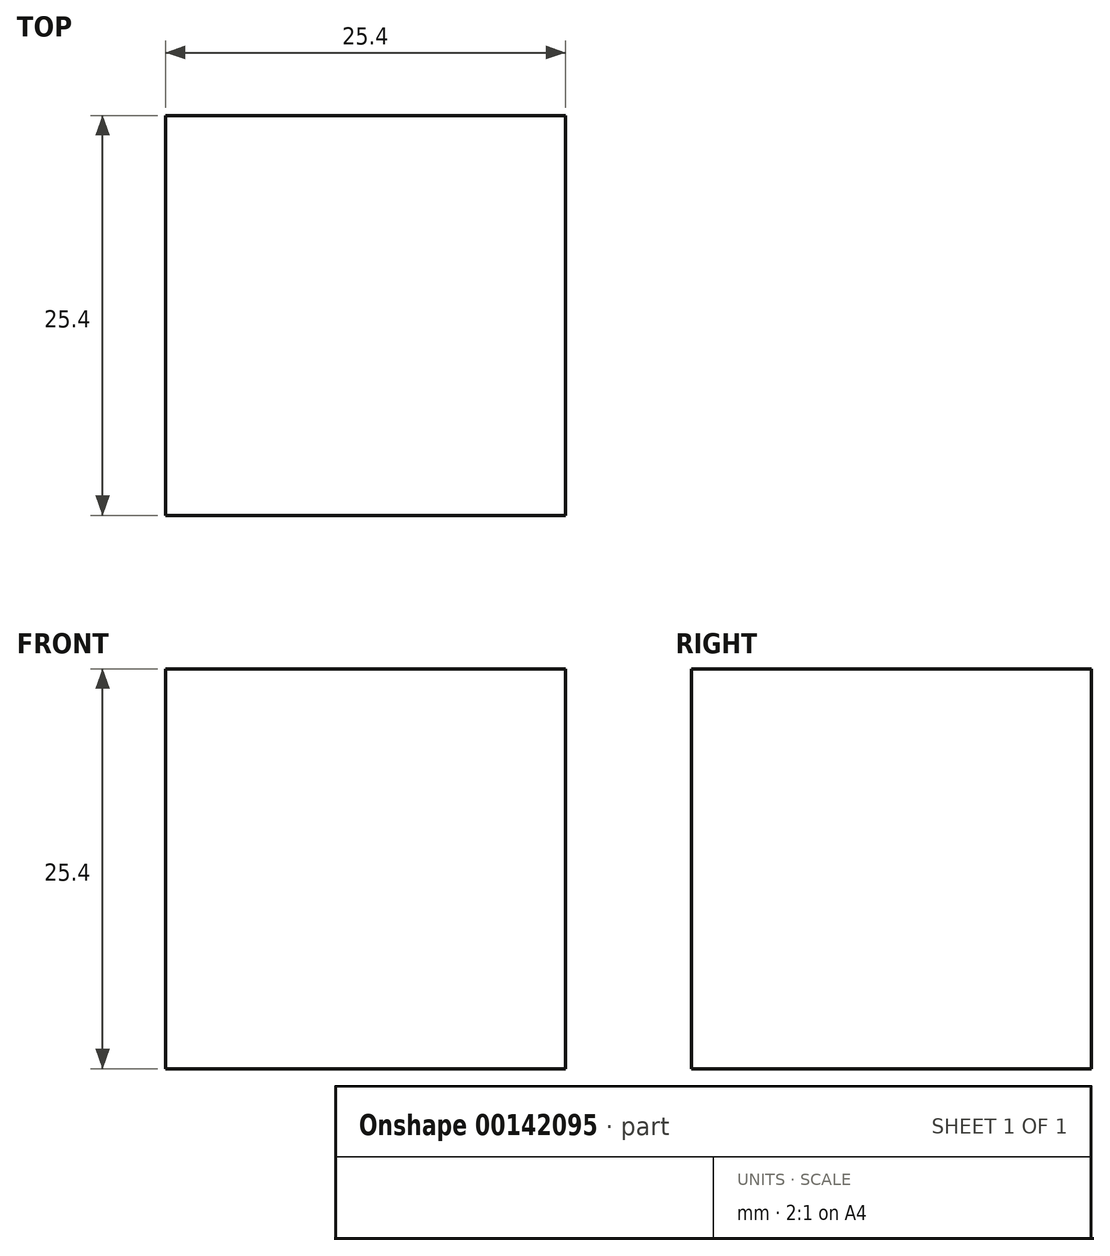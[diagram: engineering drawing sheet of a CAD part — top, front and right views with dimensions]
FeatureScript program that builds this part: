
annotation { "Feature Type Name" : "Feature", "Feature Type Description" : "" }
export const myFeature = defineFeature(function(context is Context, id is Id, definition is map)
    precondition{}
    {
        {
            var Q0;
            Q0=qCreatedBy(makeId("Top.planeOp"),FACE);
            var sketch = newSketch(context, id + "F0", { "sketchPlane" : qUnion([Q0])});
            skLineSegment(sketch, "E0.bottom", {"start": v(12.7, 12.7) * mm, "end": v(-12.7, 12.7) * mm});
            skLineSegment(sketch, "E0.top", {"start": v(12.7, -12.7) * mm, "end": v(-12.7, -12.7) * mm});
            skLineSegment(sketch, "E0.left", {"start": v(12.7, 12.7) * mm, "end": v(12.7, -12.7) * mm});
            skLineSegment(sketch, "E0.right", {"start": v(-12.7, 12.7) * mm, "end": v(-12.7, -12.7) * mm});
            skPoint(sketch, "E0.middle", {"position": v(0, 0) * mm});
            skSolve(sketch);
        }
        {
            var Q0;
            Q0=makeQuery(id+"F0.imprint","IMPRINT",FACE,{"disambiguationData":[TD([[makeQuery(id+"F0.imprint","IMPRINT",EDGE,{"derivedFrom":sQuery(id+"F0.wireOp",EDGE,"E0.bottom")}),1.0]])]});
            extrude(context, id + "F1", {"entities" : qUnion([Q0]), "depth" : 25.4 * mm, "symmetric" : true});
        }
    });
